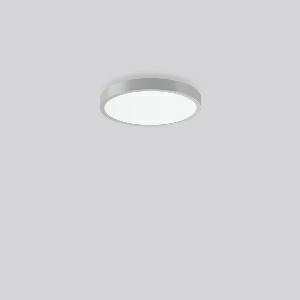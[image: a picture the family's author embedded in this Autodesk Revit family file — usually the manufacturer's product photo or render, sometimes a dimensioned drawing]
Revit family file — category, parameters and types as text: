
# Revit family: triona_round_a_312420_004_2_730_b341
name_source: partatom
category: Lighting Fixtures
units: mm (PartAtom-declared; Revit-internal decimal feet)

## family parameters
Cut with Voids When Loaded = No
Host = Face
Light Source = No
Part Type = Normal
Room Calculation Point = No
Round Connector Dimension = Use Diameter
Shared = No

## types (1)
- TuneableWhite 846 (1 x LED Modul 846, 3050 lm, 4600)
    Apparent Load = 38 VA
    CIE Flux Codes = 48 79 96 82 100
    Color Rendering = 80
    Color Temperature = 4600
    Default Elevation = 1800 mm
    Description = Series: TRIONA round
Decorative round LED surface-mounted luminaire. Flat, seamless frame: aluminium extrusion profile, powder coated. Cover made of sheet steel, powder-coated. Direct light emission through a diffuser plastic opal. Indirect light emission through a flush diffuser made of satin-finish plastic. Lightguide and diffuser made of non-yellowing plastic (PMMA). Lateral light emission (RZB SIDELITE technology) for above-average homogeneous light distribution. Direct 70%, indirect 30% light emission. Tunable white versions, dynamically adjustable from 2700 K to 6500 K. Suitable for Ceiling mounting, Wall (surface). Tool-free mounting via bayonet connection. Electronic ballast included. Very easy installation thanks to Plug+Play connection. With Casambi smart+free Bluetooth control for wireless network and operation using Android / iOS devices, free app available for download. Ideal for use as part of the Human Centric Lighting concept in connection with RZB light management systems. 
Colour: silver, matt (approx. RAL 9006)
Diameter: 461 mm
Height: 88 mm
Lamp: LED
Socket: without socket
Colour temperature: 2700K - 6500K
Colour rendering index (CRI): 80
System power: 38 W
Rated luminous flux: 3050 lm
Luminous efficiency: 80 lm/W
System power 2: 39 W
Rated luminous flux 2: 2900 lm
Luminous efficiency 2: 74 lm/W
System power 3: 39 W
Rated luminous flux 3: 2950 lm
Luminous efficiency 3: 76 lm/W
Control gear: Dimmable Bluetooth converter
Protection class: I
Type of protection: IP 20
    Height = 88 mm
    Lamp = 1 x LED Modul 846
    Lamp Light Flux = 3050 lm
    Lamp count = 1
    Length = 461 mm
    Lifetime = 50000 h
    Luminous efficacy = 80 lm/W
    Manufacturer = RZB
    ModVariant = No
    Model = 312420.004.2.730
    Mounting Place = Ceiling
    Mounting Type = Surface mounted
    Number of Poles = 1
    OnlyDefault = Yes
    Power Factor = 1
    Product Name = TRIONA round A
    Product group = Surface mounted modular luminaires
    ProductGroupID = 306
    Protection Class = Protection class I
    Protection Degree = IP 20
    RLX_Detail_Level = 1
    RLX_Emergency_Light_Flux = 0 lm
    RLX_Emergency_Type = 0
    RLX_Emergency_Type_DB = No
    RlxData = <blob elided: 39537 chars, md5=2eef87d8>
    Socket = socket
    Standby Power = 0 W
    System Light Flux = 3050 lm
    System Power = 38 W
    Type Comments = TuneableWhite 846
    Type Image = 312420.004.jpg
    URL = http://relux.com
    VarID = tuneablewhite_846
    Voltage = 230 V
    Voltage Range = 220-240 V
    Weight = 0.00 kg
    Width = 0 mm  [stored 0 ft]

note: [stored X ft] marks values corroborated as IEEE doubles in the binary element streams (Revit-internal decimal feet)

## geometry (parser evidence)
native form markers: Blend x4, Sweep x12
no freeform markers — native parametric forms only
